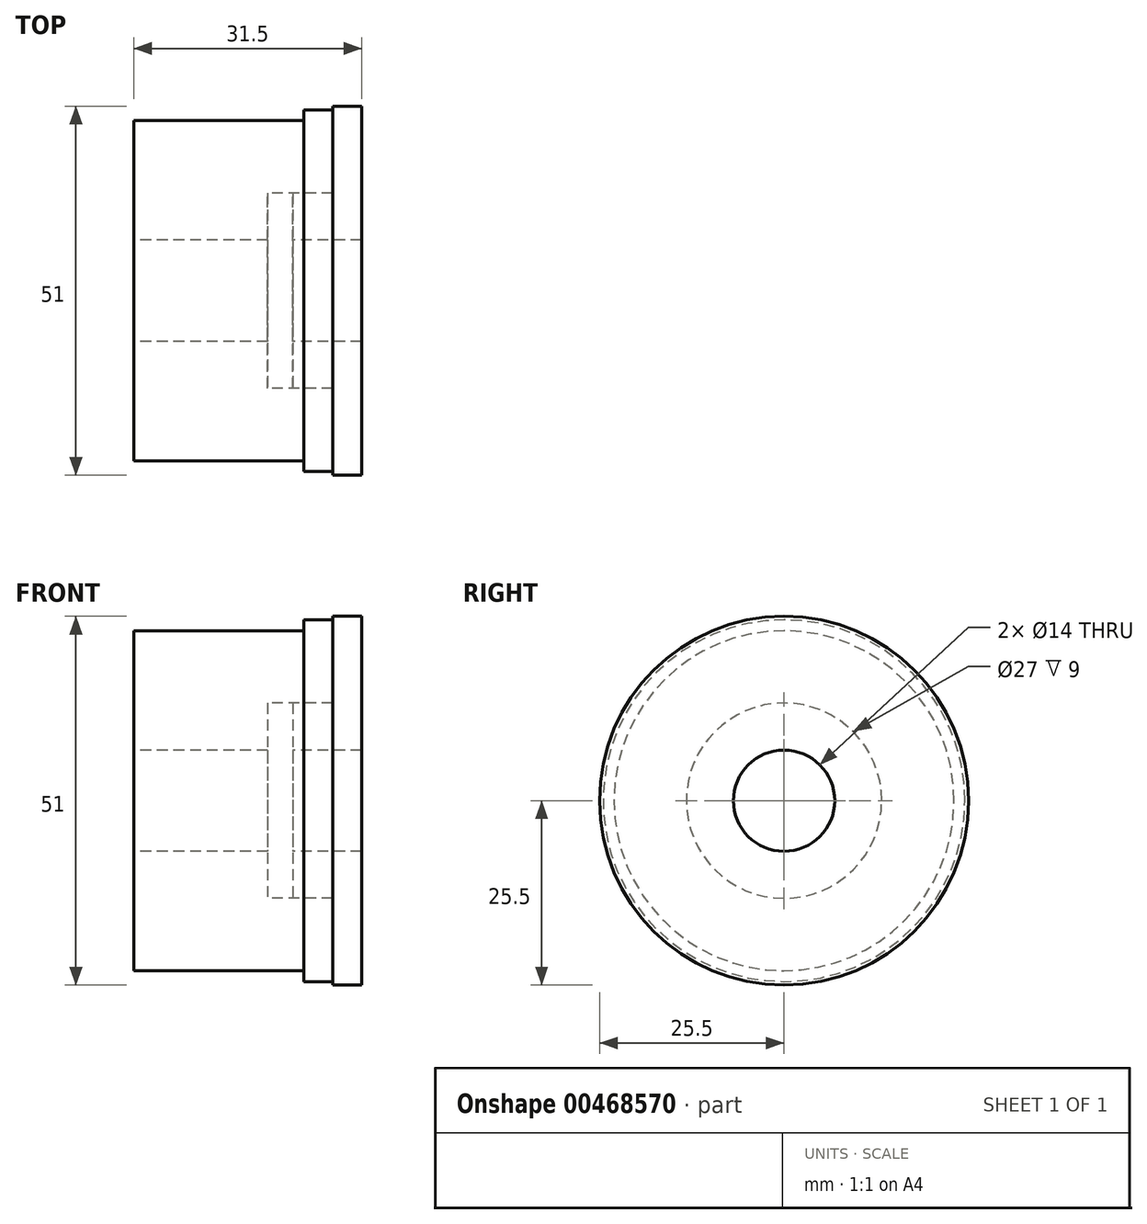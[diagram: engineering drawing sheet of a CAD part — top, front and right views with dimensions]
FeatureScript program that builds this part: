
annotation { "Feature Type Name" : "Feature", "Feature Type Description" : "" }
export const myFeature = defineFeature(function(context is Context, id is Id, definition is map)
    precondition{}
    {
        {
            var Q0;
            Q0=qCreatedBy(makeId("Front.planeOp"),FACE);
            var sketch = newSketch(context, id + "F0", { "sketchPlane" : qUnion([Q0])});
            skLineSegment(sketch, "E0", {"start": v(0, 0) * mm, "end": v(27.5, 0) * mm});
            skLineSegment(sketch, "E1", {"start": v(27.5, 0) * mm, "end": v(27.5, 25) * mm});
            skLineSegment(sketch, "E2", {"start": v(27.5, 25) * mm, "end": v(23.5, 25) * mm});
            skLineSegment(sketch, "E3", {"start": v(0, 0) * mm, "end": v(0, 23.5) * mm});
            skLineSegment(sketch, "E4", {"start": v(0, 23.5) * mm, "end": v(23.5, 23.5) * mm});
            skLineSegment(sketch, "E5", {"start": v(23.5, 23.5) * mm, "end": v(23.5, 25) * mm});
            skLineSegment(sketch, "E6", {"start": v(27.5, 7) * mm, "end": v(0, 7) * mm});
            skPoint(sketch, "E7", {"position": v(27.5, 13.5) * mm});
            skLineSegment(sketch, "E8", {"start": v(27.5, 13.5) * mm, "end": v(18.5, 13.5) * mm});
            skLineSegment(sketch, "E9", {"start": v(18.5, 13.5) * mm, "end": v(18.5, 7) * mm});
            skSolve(sketch);
        }
        {
            var Q0;
            {var subQ3=sQuery(id+"F0.wireOp",EDGE,"E2");Q0=makeQuery(id+"F0.imprint","IMPRINT",FACE,{"disambiguationData":[TD([[makeQuery(id+"F0.imprint","IMPRINT",EDGE,{"derivedFrom":subQ3}),1.0]])]});}
            var Q1;
            Q1=sQuery(id+"F0.wireOp",EDGE,"E0");
            revolve(context, id + "F1", {"surfaceOperationType" : NewSurfaceOperationType.NEW, "entities" : qUnion([Q0]), "axis" : qUnion([Q1]), "revolveType" : RevolveType.FULL});
        }
        {
            var Q0;
            Q0=qCreatedBy(makeId("Front.planeOp"),FACE);
            var sketch = newSketch(context, id + "F2", { "sketchPlane" : qUnion([Q0])});
            skLineSegment(sketch, "E10.0", {"start": v(27.5, -13.5) * mm, "end": v(27.5, 13.5) * mm});
            skLineSegment(sketch, "E11", {"start": v(27.5, 13.5) * mm, "end": v(22, 13.5) * mm});
            skLineSegment(sketch, "E12", {"start": v(22, 13.5) * mm, "end": v(22, 0) * mm});
            skLineSegment(sketch, "E13", {"start": v(22, 0) * mm, "end": v(31.5, 0) * mm});
            skLineSegment(sketch, "E14", {"start": v(31.5, 0) * mm, "end": v(31.5, 25.5) * mm});
            skLineSegment(sketch, "E15", {"start": v(31.5, 25.5) * mm, "end": v(27.5, 25.5) * mm});
            skLineSegment(sketch, "E16", {"start": v(27.5, 25.5) * mm, "end": v(27.5, 0) * mm});
            skLineSegment(sketch, "E17", {"start": v(31.5, 7) * mm, "end": v(22, 7) * mm});
            skSolve(sketch);
        }
        {
            var Q0;
            {var subQ4=sQuery(id+"F2.wireOp",EDGE,"E15");Q0=makeQuery(id+"F2.imprint","IMPRINT",FACE,{"disambiguationData":[TD([[makeQuery(id+"F2.imprint","IMPRINT",EDGE,{"derivedFrom":subQ4}),1.0]])]});}
            var Q1;
            {var subQ0=sQuery(id+"F2.wireOp",EDGE,"E11");Q1=makeQuery(id+"F2.imprint","IMPRINT",FACE,{"disambiguationData":[TD([[makeQuery(id+"F2.imprint","IMPRINT",EDGE,{"derivedFrom":subQ0}),1.0]])]});}
            var Q2;
            Q2=sQuery(id+"F2.wireOp",EDGE,"E13");
            revolve(context, id + "F3", {"surfaceOperationType" : NewSurfaceOperationType.NEW, "entities" : qUnion([Q0, Q1]), "axis" : qUnion([Q2]), "revolveType" : RevolveType.FULL});
        }
    });
